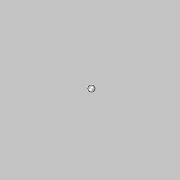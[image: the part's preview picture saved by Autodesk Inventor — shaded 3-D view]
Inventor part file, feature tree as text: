
AUTODESK INVENTOR PART (.ipt)
format: ipt  version: 2017 (Build 210142000, 142)  size: 100,864 bytes
history: native  units: mm
features: other x10, sketch x2, extrude x2, pattern_linear x2, sweep x1, plane x1
ambient origin geometry x7: Origin, YZ Plane, XZ Plane, X Axis, Y Axis, Z Axis, Center Point
feature tree (18):
  other  "Table"
  other  "WireMeshCableTrayRVS60x60"
  other  "WireMeshCableTrayRVS60x100"
  other  "WireMeshCableTrayRVS60x200"
  other  "WireMeshCableTrayRVS60x400"
  other  "WireMeshCableTrayRVS60x600"
  other  "WireMeshCableTrayRVS100x150"
  other  "WireMeshCableTrayRVS100x300"
  sketch  "Sketch6"  dims[d22=5.0mm d23=10.0mm]
  extrude  "Extrusion4"  Depth=10.0mm
  sweep  "Sweep1"
  extrude  "Extrusion5"  TaperAngle=0.0deg  [1 undecoded]
  pattern_linear  "Rectangular Pattern2"  Count1=300 Spacing1=0.0mm
  pattern_linear  "Rectangular Pattern3"  Count1=5 Spacing1=0.0mm
  plane  "Work Plane2"
  other  "XY Ground Plane"
  sketch  "Sketch7"  dims[d24=3000.0mm d25=0.0mm d26=5.0mm d27=0.0mm d28=0.0mm d29=3000.0mm d30=0.0mm d31=0.0mm d33=50.0mm d34=310.0mm d36=100.0mm d39=180.0deg d40=2.5mm]
  other  "Work Axis1"
note: 1 required parameter value undecoded (feature->parameter linkage not recoverable at this tier; creation-order binding heuristic only, values carry confidence <= 0.55)
